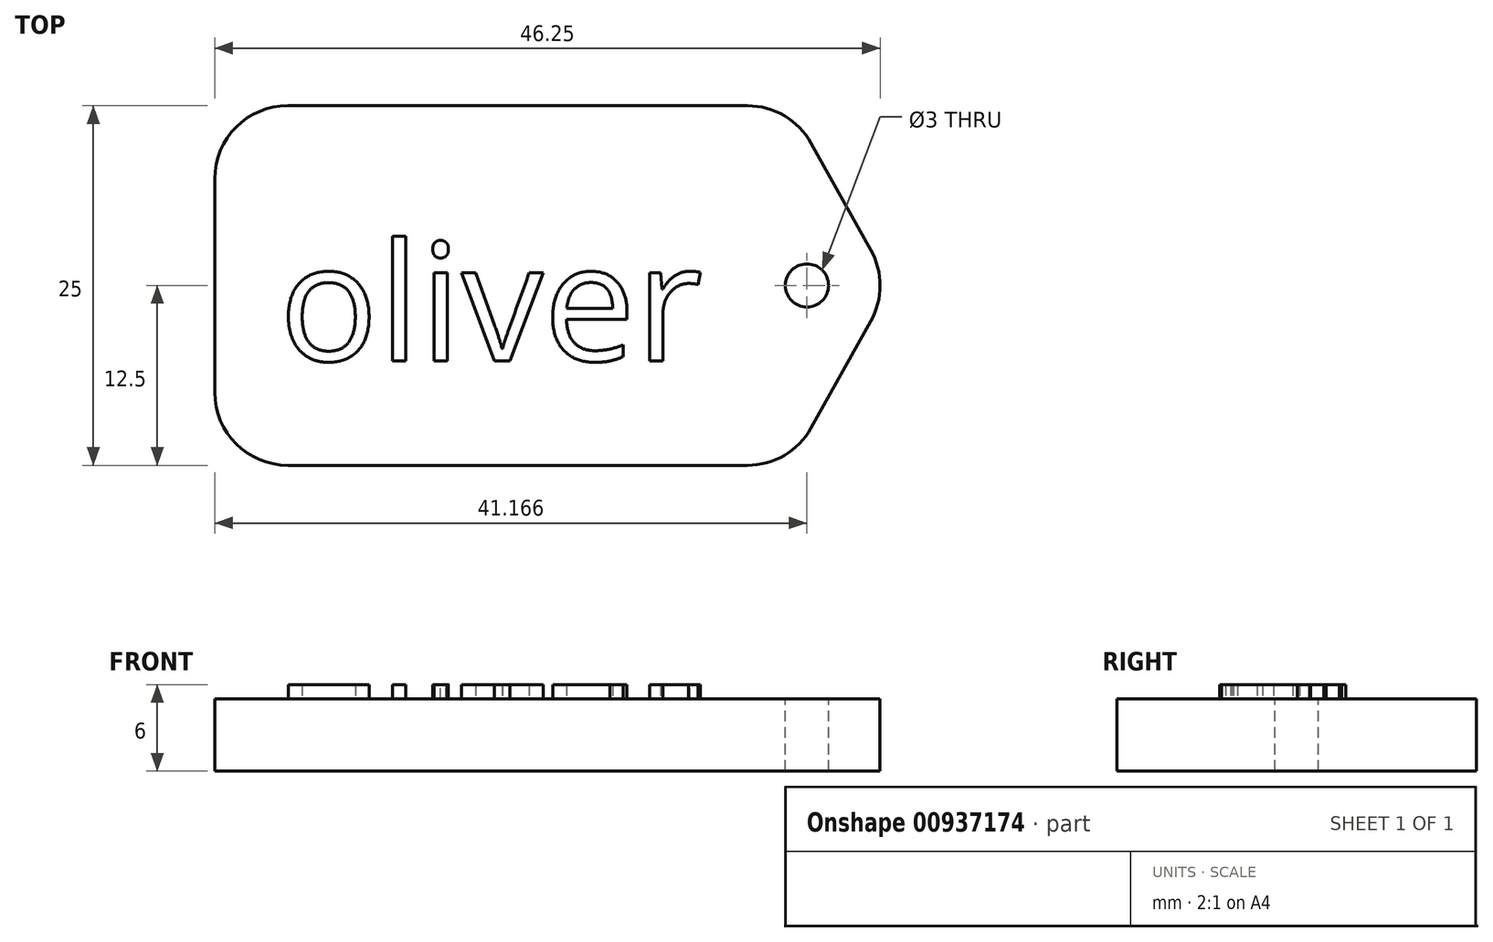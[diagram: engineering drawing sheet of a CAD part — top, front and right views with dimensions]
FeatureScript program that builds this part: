
annotation { "Feature Type Name" : "Feature", "Feature Type Description" : "" }
export const myFeature = defineFeature(function(context is Context, id is Id, definition is map)
    precondition{}
    {
        {
            var Q0;
            Q0=qCreatedBy(makeId("Top.planeOp"),FACE);
            var sketch = newSketch(context, id + "F0", { "sketchPlane" : qUnion([Q0])});
            skLineSegment(sketch, "E0.bottom", {"start": v(-20, -12.5) * mm, "end": v(20, -12.5) * mm});
            skLineSegment(sketch, "E0.top", {"start": v(-20, 12.5) * mm, "end": v(20, 12.5) * mm});
            skLineSegment(sketch, "E0.left", {"start": v(-20, -12.5) * mm, "end": v(-20, 12.5) * mm});
            skPoint(sketch, "E0.middle", {"position": v(0, 0) * mm});
            skPoint(sketch, "E1", {"position": v(26.99, 0) * mm});
            skLineSegment(sketch, "E2", {"start": v(20, 12.5) * mm, "end": v(26.99, 0) * mm});
            skLineSegment(sketch, "E3", {"start": v(20, -12.5) * mm, "end": v(26.99, 0) * mm});
            skSolve(sketch);
        }
        {
            var Q0;
            Q0 = qSketchRegion(id + "F0", true);
            extrude(context, id + "F1", {"entities" : qUnion([Q0]), "depth" : 5 * mm, "offsetDistance" : 25.4 * mm});
        }
        {
            var Q0;
            Q0=makeQuery(id+"F1.opExtrude","SWEPT_EDGE",EDGE,{"disambiguationData":[OSD([sQuery(id+"F0.wireOp",EDGE,"E2"),sQuery(id+"F0.wireOp",EDGE,"E3")])]});
            fillet(context, id + "F2", {"entities" : qUnion([Q0]), "radius" : 5.08 * mm, "tangentPropagation" : true, "allowEdgeOverflow" : false});
        }
        {
            var Q0;
            Q0=makeQuery(id+"F1.opExtrude","CAP_FACE",FACE,{"disambiguationData":[OSD([sQuery(id+"F0.wireOp",EDGE,"E0.bottom"),sQuery(id+"F0.wireOp",EDGE,"E0.top"),sQuery(id+"F0.wireOp",EDGE,"E0.left"),sQuery(id+"F0.wireOp",EDGE,"E2"),sQuery(id+"F0.wireOp",EDGE,"E3")])],"isStart":false});
            var sketch = newSketch(context, id + "F3", { "sketchPlane" : qUnion([Q0])});
            skPoint(sketch, "E4", {"position": v(0, 0) * mm});
            skPoint(sketch, "E5", {"position": v(21.17, 0) * mm});
            skSolve(sketch);
        }
        {
            var Q0;
            Q0=sQuery(id+"F3.wireOp",VERTEX,"E5");
            var Q1;
            Q1=makeQuery(id+"F1.opExtrude","SWEPT_BODY",BODY,{"disambiguationData":[OSD([sQuery(id+"F0.wireOp",EDGE,"E0.bottom"),sQuery(id+"F0.wireOp",EDGE,"E0.top"),sQuery(id+"F0.wireOp",EDGE,"E0.left"),sQuery(id+"F0.wireOp",EDGE,"E2"),sQuery(id+"F0.wireOp",EDGE,"E3")])]});
            hole(context, id + "F4", {"style" : HoleStyle.SIMPLE, "endStyle" : HoleEndStyle.THROUGH, "holeDiameter" : 3 * mm, "majorDiameter" : 6.35 * mm, "isTappedThrough" : true, "tappedDepth" : 12.7 * mm, "tapClearance" : 3, "locations" : qUnion([Q0]), "scope" : qUnion([Q1])});
        }
        {
            var Q0;
            Q0=makeQuery(id+"F1.opExtrude","SWEPT_EDGE",EDGE,{"disambiguationData":[OSD([sQuery(id+"F0.wireOp",EDGE,"E0.top"),sQuery(id+"F0.wireOp",EDGE,"E2")])]});
            var Q1;
            Q1=makeQuery(id+"F1.opExtrude","SWEPT_EDGE",EDGE,{"disambiguationData":[OSD([sQuery(id+"F0.wireOp",EDGE,"E0.top"),sQuery(id+"F0.wireOp",EDGE,"E0.left")])]});
            fillet(context, id + "F5", {"entities" : qUnion([Q0, Q1]), "radius" : 5.08 * mm, "tangentPropagation" : true, "allowEdgeOverflow" : false});
        }
        {
            var Q0;
            Q0=makeQuery(id+"F1.opExtrude","SWEPT_EDGE",EDGE,{"disambiguationData":[OSD([sQuery(id+"F0.wireOp",EDGE,"E0.bottom"),sQuery(id+"F0.wireOp",EDGE,"E0.left")])]});
            fillet(context, id + "F6", {"entities" : qUnion([Q0]), "radius" : 5.08 * mm, "tangentPropagation" : true, "allowEdgeOverflow" : false});
        }
        {
            var Q0;
            Q0=makeQuery(id+"F1.opExtrude","SWEPT_EDGE",EDGE,{"disambiguationData":[OSD([sQuery(id+"F0.wireOp",EDGE,"E0.bottom"),sQuery(id+"F0.wireOp",EDGE,"E3")])]});
            fillet(context, id + "F7", {"entities" : qUnion([Q0]), "radius" : 5.08 * mm, "tangentPropagation" : true, "allowEdgeOverflow" : false});
        }
        {
            var Q0;
            Q0=makeQuery(id+"F1.opExtrude","CAP_FACE",FACE,{"disambiguationData":[OSD([sQuery(id+"F0.wireOp",EDGE,"E0.bottom"),sQuery(id+"F0.wireOp",EDGE,"E0.top"),sQuery(id+"F0.wireOp",EDGE,"E0.left"),sQuery(id+"F0.wireOp",EDGE,"E2"),sQuery(id+"F0.wireOp",EDGE,"E3")])],"isStart":false});
            var sketch = newSketch(context, id + "F8", { "sketchPlane" : qUnion([Q0])});
            skText(sketch, "E6", { "text": "oliver", "fontName": "OpenSans-Regular.ttf"});
            const initialGuessF8  = {"E6": [-0.01552, -0.00523, 1, 0, 0.00821]};
            skSetInitialGuess(sketch, initialGuessF8);
            skSolve(sketch);
        }
        {
            var Q0;
            Q0 = qSketchRegion(id + "F8", true);
            extrude(context, id + "F9", {"entities" : qUnion([Q0]), "operationType" : NewBodyOperationType.ADD, "depth" : 1 * mm, "offsetDistance" : 25.4 * mm});
        }
    });
